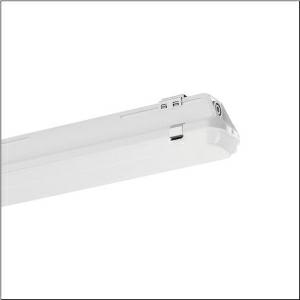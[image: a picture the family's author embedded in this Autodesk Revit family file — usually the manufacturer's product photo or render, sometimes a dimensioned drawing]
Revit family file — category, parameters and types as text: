
# Revit family: monsun_r__21_emergency_51fb10dp467c3h_775e
name_source: partatom
category: Lighting Fixtures
units: mm (PartAtom-declared; Revit-internal decimal feet)

## family parameters
Cut with Voids When Loaded = No
Host = Face
Light Source = No
Part Type = Normal
Room Calculation Point = No
Round Connector Dimension = Use Diameter
Shared = No

## types (1)
- --- (1 x LED, 6060 lm, 36.5 W, 4000K)
    Apparent Load = 37 VA
    CIE Flux Codes = 47 77 93 94 100
    Color Rendering = 80
    Color Temperature = 4000K
    Default Elevation = 1800 mm
    Description = Monsun® 21 emergency, damp-proof luminaire, chain hanger, primary optical cover: enclosure, of PMMA, light emission: direct distribution, primary light characteristic: symmetric, installation type: vertical mounting, horizontal mounting, surface-mounted, suspended mounting, LED, rated luminous flux: 6.060lm, luminous efficacy: 185lm/W, light colour: 840, colour temperature: 4000K, control gear: DALI 2, with terminal, 5+3-pole, max. 2.5mm², mains connection: 220..240V, AC, 50/60Hz, rated input power: 37W, control gear: single battery element, battery: LiFePO4, 9Ah, housing, of glass-fibre reinforced polyester, uncoated, bright grey, incl. chain hanger, length: 1.590mm, width: 90mm, height: 88mm, clip for enclosure, of stainless steel (V2A), ceiling mounting element, of stainless steel (V2A), chain hanger, of stainless steel (V2A), protection rating (complete): IP66, insulation class (complete): insulation class I (protective earthing), certification: CE, UKCA, protection symbol: D, impact resistance: IK04, permissible operating ambient temperature: +5..+25°C, standard: EN 50419, EN 60598-2-1, EN 60598-2-22, corresponds to IFS (International Featured Standards) requirements for safety and quality in the food industry, for indoor or canopied outdoor use, no direct snow, no direct sun, no direct rain, LABS conformity tested according to VDMA 24364:2018-05, contact your sales advisor before using the luminaires in applications with unclear chemical exposure, large temperature fluctuations or condensation-forming humidity, packaging unit: 1 piece
    Height = 89 mm
    Lamp = 1 x LED
    Lamp Light Flux = 6060 lm
    Lamp Power = 36.5 W
    Lamp count = 1
    Length = 1590 mm
    Luminous efficacy = 166 lm/W
    Manufacturer = Siteco
    ModVariant = No
    Model = 51FB10DP467C3H
    Mounting Place = Ceiling
    Mounting Type = Surface mounted
    Number of Poles = 1
    OnlyDefault = Yes
    Power Factor = 1
    Product Name = Monsun® 21 emergency
    Product group = damp-proof luminaire
    ProductGroupID = 300
    Protection Class = Protection class I
    Protection Degree = IP 66
    RLX_Detail_Level = 1
    RLX_Emergency_Light_Flux = 0 lm
    RLX_Emergency_Type = 0
    RLX_Emergency_Type_DB = No
    RlxData = <blob elided: 92165 chars, md5=2e2f0ee6>
    Socket = socket
    Standby Power = 0 W
    System Light Flux = 6060 lm
    System Power = 37 W
    Type Comments = : luminous flux: 100 % | dim-lin: 254 | 229 mA
    Type Image = l_1319656.jpg
    URL = http://relux.com
    VarID = @adj_031634
    Voltage = 0 V
    Weight = 0.00 kg
    Width = 90 mm

## geometry (parser evidence)
native form markers: Blend x4, Sweep x14
no freeform markers — native parametric forms only
